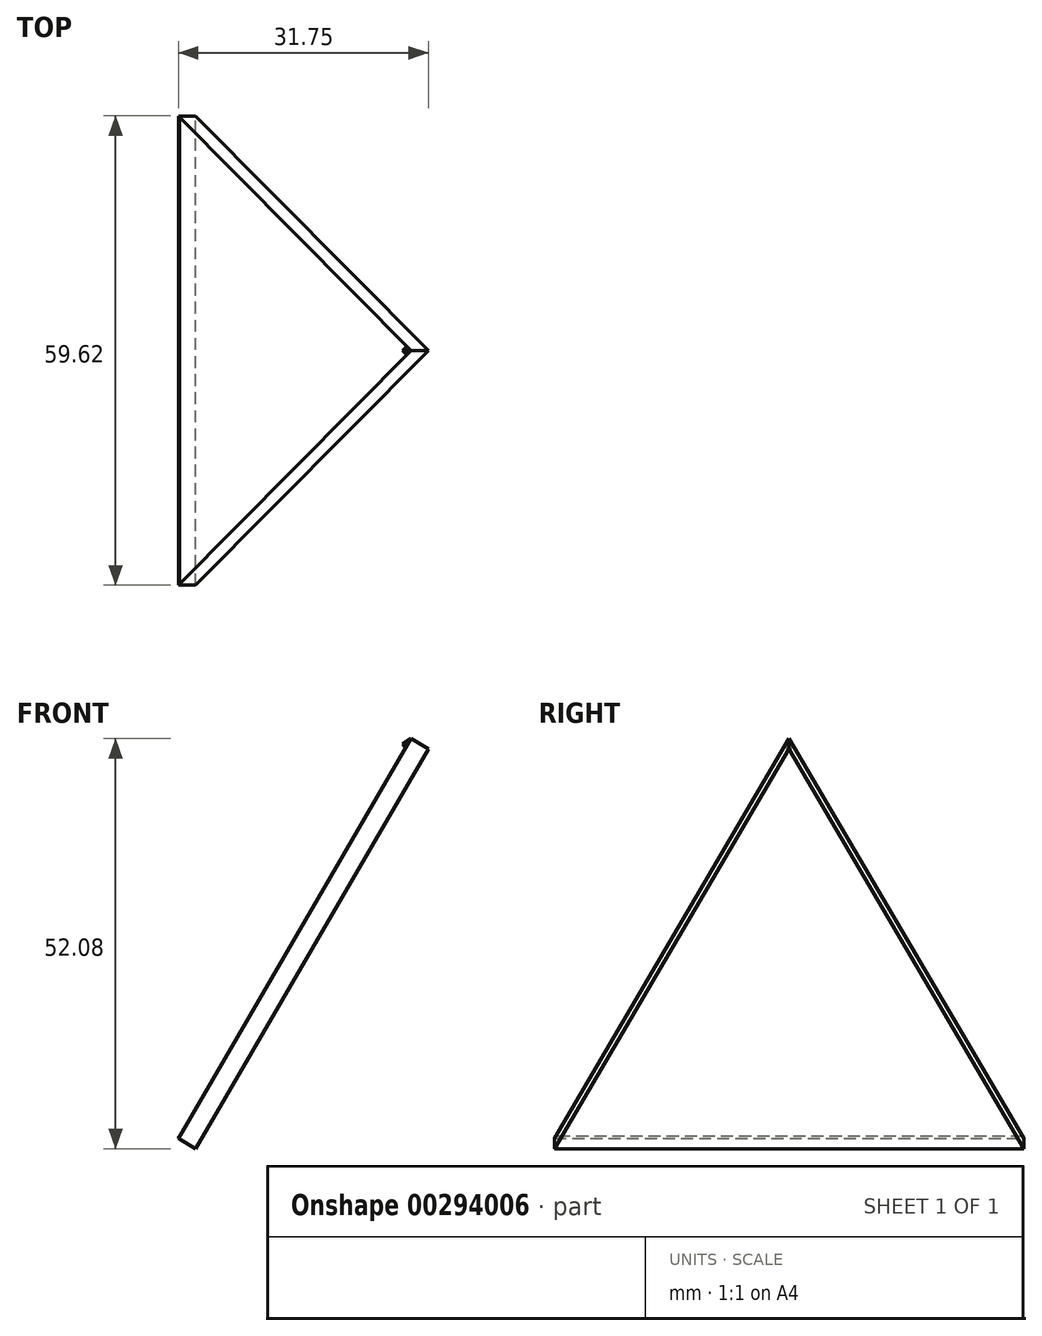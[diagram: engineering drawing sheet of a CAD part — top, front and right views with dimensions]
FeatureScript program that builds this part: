
annotation { "Feature Type Name" : "Feature", "Feature Type Description" : "" }
export const myFeature = defineFeature(function(context is Context, id is Id, definition is map)
    precondition{}
    {
        {
            var Q0;
            Q0=qCreatedBy(makeId("Top.planeOp"),FACE);
            var sketch = newSketch(context, id + "F0", { "sketchPlane" : qUnion([Q0])});
            skLineSegment(sketch, "E0.bottom", {"start": v(-29.55, 29.8) * mm, "end": v(29.55, 29.8) * mm});
            skLineSegment(sketch, "E0.top", {"start": v(-29.55, -29.8) * mm, "end": v(29.55, -29.8) * mm});
            skLineSegment(sketch, "E0.left", {"start": v(-29.55, 29.8) * mm, "end": v(-29.55, -29.8) * mm});
            skLineSegment(sketch, "E0.right", {"start": v(29.55, 29.8) * mm, "end": v(29.55, -29.8) * mm});
            skPoint(sketch, "E0.middle", {"position": v(0, 0) * mm});
            skSolve(sketch);
        }
        {
            var Q0;
            Q0=qCreatedBy(makeId("Top.planeOp"),FACE);
            cPlane(context, id + "F1", {"entities" : qUnion([Q0]), "cplaneType" : CPlaneType.OFFSET, "offset" : 50.8 * mm, "width" : 152.4 * mm, "height" : 152.4 * mm});
        }
        {
            var Q0;
            Q0=qCreatedBy(id+"F1.planeOp",FACE);
            var sketch = newSketch(context, id + "F2", { "sketchPlane" : qUnion([Q0])});
            skPoint(sketch, "E1", {"position": v(0, 0) * mm});
            skSolve(sketch);
        }
        {
            var Q0;
            Q0=sQuery(id+"F2.wireOp",VERTEX,"E1");
            var Q1;
            Q1=sQuery(id+"F0.wireOp",EDGE,"E0.left");
            cPlane(context, id + "F3", {"entities" : qUnion([Q0, Q1]), "cplaneType" : CPlaneType.LINE_ANGLE, "offset" : 25.4 * mm, "angle" : 0 * degree, "width" : 152.4 * mm, "height" : 152.4 * mm});
        }
        {
            var Q0;
            Q0=qCreatedBy(id+"F3.planeOp",FACE);
            var sketch = newSketch(context, id + "F4", { "sketchPlane" : qUnion([Q0])});
            skLineSegment(sketch, "E2", {"start": v(-29.8, -14.85) * mm, "end": v(0, 43.91) * mm});
            skLineSegment(sketch, "E3", {"start": v(0, 43.91) * mm, "end": v(29.8, -14.85) * mm});
            skLineSegment(sketch, "E4", {"start": v(29.8, -14.85) * mm, "end": v(-29.8, -14.85) * mm});
            skSolve(sketch);
        }
        {
            var Q0;
            Q0=sQuery(id+"F0.wireOp",EDGE,"E0.top");
            var Q1;
            Q1=sQuery(id+"F2.wireOp",VERTEX,"E1");
            cPlane(context, id + "F5", {"entities" : qUnion([Q0, Q1]), "cplaneType" : CPlaneType.LINE_ANGLE, "offset" : 25.4 * mm, "angle" : 0 * degree, "width" : 152.4 * mm, "height" : 152.4 * mm});
        }
        {
            var Q0;
            Q0=qCreatedBy(id+"F5.planeOp",FACE);
            var sketch = newSketch(context, id + "F6", { "sketchPlane" : qUnion([Q0])});
            skLineSegment(sketch, "E5", {"start": v(-29.55, -15.08) * mm, "end": v(29.55, -15.08) * mm});
            skLineSegment(sketch, "E6", {"start": v(29.55, -15.08) * mm, "end": v(0, 43.81) * mm});
            skLineSegment(sketch, "E7", {"start": v(0, 43.81) * mm, "end": v(-29.55, -15.08) * mm});
            skSolve(sketch);
        }
        {
            var Q0;
            Q0=sQuery(id+"F0.wireOp",EDGE,"E0.bottom");
            var Q1;
            Q1=sQuery(id+"F2.wireOp",VERTEX,"E1");
            cPlane(context, id + "F7", {"entities" : qUnion([Q0, Q1]), "cplaneType" : CPlaneType.LINE_ANGLE, "offset" : 25.4 * mm, "angle" : 0 * degree, "width" : 152.4 * mm, "height" : 152.4 * mm});
        }
        {
            var Q0;
            Q0=qCreatedBy(id+"F7.planeOp",FACE);
            var sketch = newSketch(context, id + "F8", { "sketchPlane" : qUnion([Q0])});
            skLineSegment(sketch, "E8", {"start": v(29.55, -15.08) * mm, "end": v(-29.55, -15.08) * mm});
            skLineSegment(sketch, "E9", {"start": v(-29.55, -15.08) * mm, "end": v(0, 43.81) * mm});
            skLineSegment(sketch, "E10", {"start": v(0, 43.81) * mm, "end": v(29.55, -15.08) * mm});
            skSolve(sketch);
        }
        {
            var Q0;
            Q0=sQuery(id+"F0.wireOp",EDGE,"E0.right");
            var Q1;
            Q1=sQuery(id+"F2.wireOp",VERTEX,"E1");
            cPlane(context, id + "F9", {"entities" : qUnion([Q0, Q1]), "cplaneType" : CPlaneType.LINE_ANGLE, "offset" : 25.4 * mm, "angle" : 0 * degree, "width" : 152.4 * mm, "height" : 152.4 * mm});
        }
        {
            var Q0;
            Q0=qCreatedBy(id+"F9.planeOp",FACE);
            var sketch = newSketch(context, id + "F10", { "sketchPlane" : qUnion([Q0])});
            skLineSegment(sketch, "E11", {"start": v(29.8, -14.85) * mm, "end": v(-29.8, -14.85) * mm});
            skLineSegment(sketch, "E12", {"start": v(-29.8, -14.85) * mm, "end": v(0, 43.91) * mm});
            skLineSegment(sketch, "E13", {"start": v(0, 43.91) * mm, "end": v(29.8, -14.85) * mm});
            skSolve(sketch);
        }
        {
            var Q0;
            Q0=makeQuery(id+"F10.imprint","IMPRINT",FACE,{"disambiguationData":[TD([[makeQuery(id+"F10.imprint","IMPRINT",EDGE,{"derivedFrom":sQuery(id+"F10.wireOp",EDGE,"E11")}),-1.0]])]});
            extrude(context, id + "F11", {"entities" : qUnion([Q0]), "endBound" : BoundingType.SYMMETRIC, "depth" : 2.54 * mm});
        }
        {
            var Q0;
            Q0=makeQuery(id+"F0.imprint","IMPRINT",FACE,{"disambiguationData":[TD([[makeQuery(id+"F0.imprint","IMPRINT",EDGE,{"derivedFrom":sQuery(id+"F0.wireOp",EDGE,"E0.bottom")}),-1.0]])]});
            extrude(context, id + "F12", {"entities" : qUnion([Q0]), "depth" : 0.25 * mm});
        }
        {
            var Q0;
            Q0=makeQuery(id+"F4.imprint","IMPRINT",FACE,{"disambiguationData":[TD([[makeQuery(id+"F4.imprint","IMPRINT",EDGE,{"derivedFrom":sQuery(id+"F4.wireOp",EDGE,"E2")}),-1.0]])]});
            extrude(context, id + "F13", {"entities" : qUnion([Q0]), "operationType" : NewBodyOperationType.INTERSECT, "depth" : 25.4 * mm});
        }
        {
            var Q0;
            Q0=makeQuery(id+"F4.imprint","IMPRINT",FACE,{"disambiguationData":[TD([[makeQuery(id+"F4.imprint","IMPRINT",EDGE,{"derivedFrom":sQuery(id+"F4.wireOp",EDGE,"E2")}),-1.0]])]});
            extrude(context, id + "F14", {"entities" : qUnion([Q0]), "oppositeDirection" : true, "depth" : 2.54 * mm});
        }
    });
